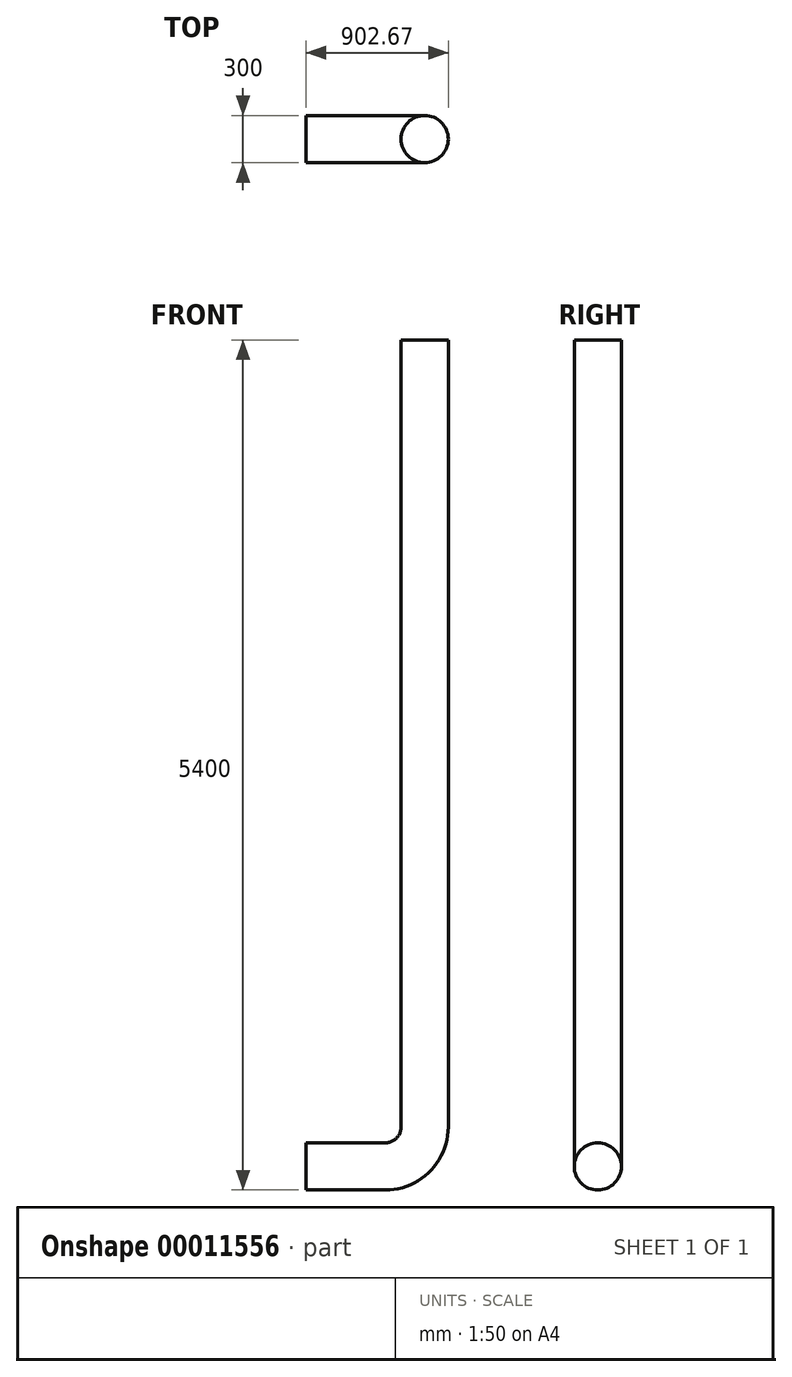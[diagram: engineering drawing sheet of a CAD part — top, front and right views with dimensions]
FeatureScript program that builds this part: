
annotation { "Feature Type Name" : "Feature", "Feature Type Description" : "" }
export const myFeature = defineFeature(function(context is Context, id is Id, definition is map)
    precondition{}
    {
        {
            var Q0;
            Q0=qCreatedBy(makeId("Right.planeOp"),FACE);
            var sketch = newSketch(context, id + "F0", { "sketchPlane" : qUnion([Q0])});
            skCircle(sketch, "E0", {"center": v(0, 0) * mm, "radius": 150 * mm});
            skSolve(sketch);
        }
        {
            var Q0;
            Q0=qCreatedBy(makeId("Front.planeOp"),FACE);
            var sketch = newSketch(context, id + "F1", { "sketchPlane" : qUnion([Q0])});
            skLineSegment(sketch, "E1", {"start": v(0, 0) * mm, "end": v(502.67, 0) * mm});
            skLineSegment(sketch, "E2", {"start": v(752.67, 250) * mm, "end": v(752.67, 5250) * mm});
            skArc(sketch, "E3.filletArc", {"start": v(502.67, 0) * mm, "mid": v(679.45, 73.22) * mm, "end": v(752.67, 250) * mm});
            skSolve(sketch);
        }
        {
            var Q0;
            Q0 = qSketchRegion(id + "F0", true);
            var Q1;
            Q1 = qBodyType(qCreatedBy(id + "F1" ,EDGE), BodyType.WIRE);
            sweep(context, id + "F2", {"profiles" : qUnion([Q0]), "path" : qUnion([Q1])});
        }
    });
